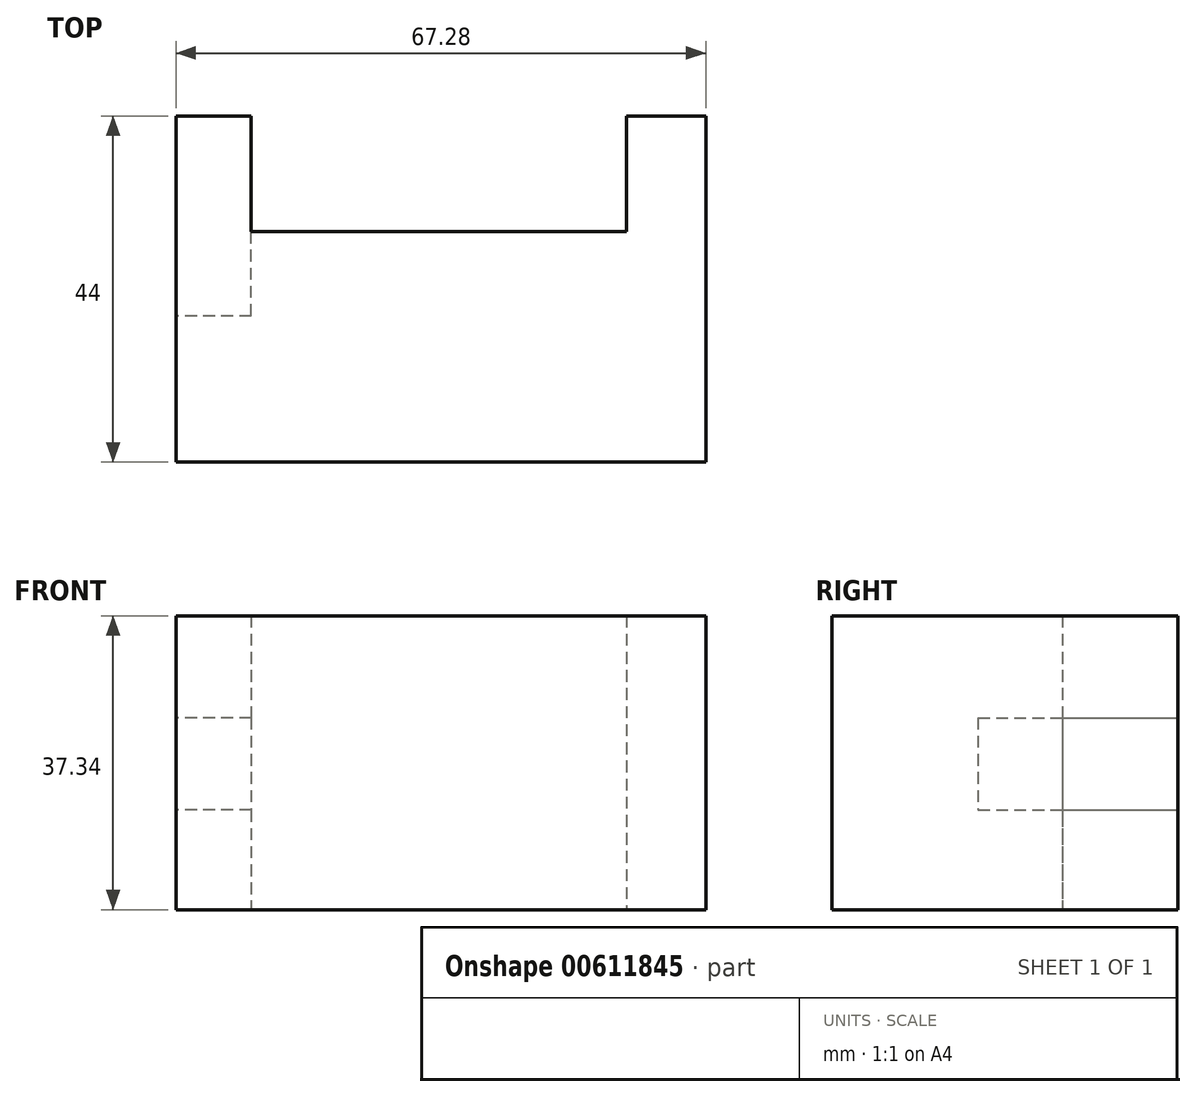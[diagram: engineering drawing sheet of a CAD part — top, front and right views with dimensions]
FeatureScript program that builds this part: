
annotation { "Feature Type Name" : "Feature", "Feature Type Description" : "" }
export const myFeature = defineFeature(function(context is Context, id is Id, definition is map)
    precondition{}
    {
        {
            var Q0;
            Q0=qCreatedBy(makeId("Top.planeOp"),FACE);
            var sketch = newSketch(context, id + "F0", { "sketchPlane" : qUnion([Q0])});
            skLineSegment(sketch, "E0.bottom", {"start": v(-33.64, 22) * mm, "end": v(-24.1, 22) * mm});
            skLineSegment(sketch, "E0.top", {"start": v(-33.64, -22) * mm, "end": v(33.64, -22) * mm});
            skLineSegment(sketch, "E0.left", {"start": v(-33.64, 22) * mm, "end": v(-33.64, -22) * mm});
            skLineSegment(sketch, "E0.right", {"start": v(33.64, 22) * mm, "end": v(33.64, -22) * mm});
            skPoint(sketch, "E0.middle", {"position": v(0, 0) * mm});
            skLineSegment(sketch, "E1.top", {"start": v(-24.1, 7.33) * mm, "end": v(23.55, 7.33) * mm});
            skLineSegment(sketch, "E1.left", {"start": v(-24.1, 22) * mm, "end": v(-24.1, 7.33) * mm});
            skLineSegment(sketch, "E1.right", {"start": v(23.55, 22) * mm, "end": v(23.55, 7.33) * mm});
            skLineSegment(sketch, "E2.trimOffspring", {"start": v(23.55, 22) * mm, "end": v(33.64, 22) * mm});
            skSolve(sketch);
        }
        {
            var Q0;
            Q0 = qSketchRegion(id + "F0", true);
            extrude(context, id + "F1", {"entities" : qUnion([Q0]), "depth" : 37.34 * mm, "offsetDistance" : 25.4 * mm});
        }
        {
            var Q0;
            Q0=makeQuery(id+"F1.opExtrude","SWEPT_FACE",FACE,{"disambiguationData":[OSD([sQuery(id+"F0.wireOp",EDGE,"E0.bottom")])]});
            var sketch = newSketch(context, id + "F2", { "sketchPlane" : qUnion([Q0])});
            skLineSegment(sketch, "E3.bottom", {"start": v(24.1, 24.38) * mm, "end": v(33.64, 24.38) * mm});
            skLineSegment(sketch, "E3.top", {"start": v(24.1, 12.65) * mm, "end": v(33.64, 12.65) * mm});
            skLineSegment(sketch, "E3.left", {"start": v(24.1, 24.38) * mm, "end": v(24.1, 12.65) * mm});
            skLineSegment(sketch, "E3.right", {"start": v(33.64, 24.38) * mm, "end": v(33.64, 12.65) * mm});
            skSolve(sketch);
        }
        {
            var Q0;
            Q0=makeQuery(id+"F2.imprint","IMPRINT",FACE,{"disambiguationData":[TD([[makeQuery(id+"F2.imprint","IMPRINT",EDGE,{"derivedFrom":sQuery(id+"F2.wireOp",EDGE,"E3.bottom")}),-1.0]])]});
            extrude(context, id + "F3", {"entities" : qUnion([Q0]), "operationType" : NewBodyOperationType.REMOVE, "oppositeDirection" : true, "depth" : 25.4 * mm, "offsetDistance" : 25.4 * mm});
        }
    });
